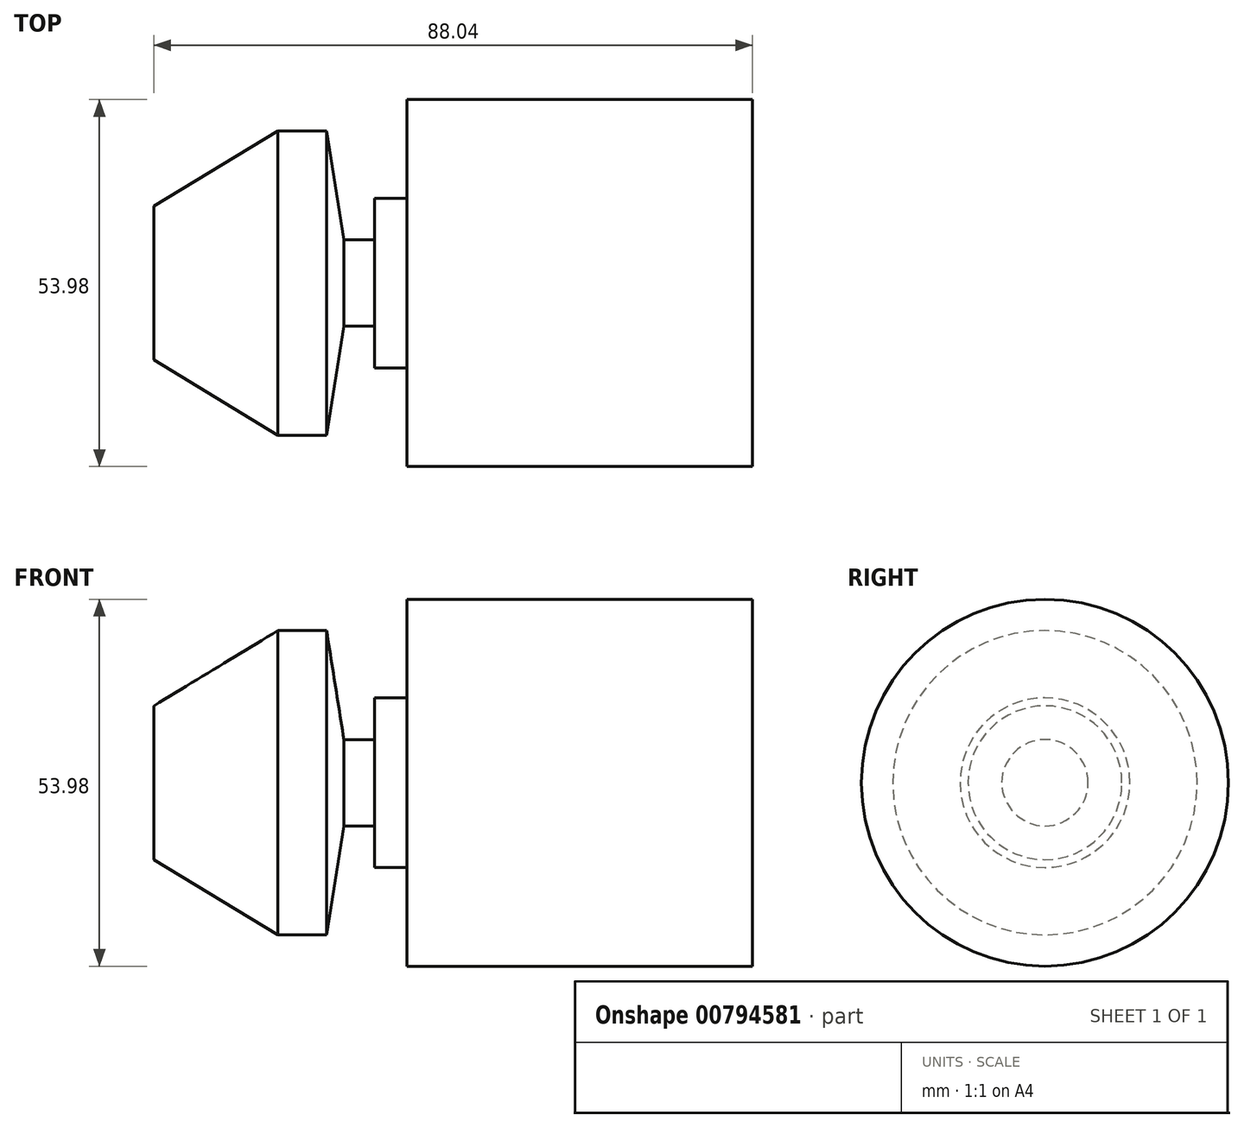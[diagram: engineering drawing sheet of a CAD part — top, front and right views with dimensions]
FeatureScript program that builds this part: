
annotation { "Feature Type Name" : "Feature", "Feature Type Description" : "" }
export const myFeature = defineFeature(function(context is Context, id is Id, definition is map)
    precondition{}
    {
        {
            var Q0;
            Q0=qCreatedBy(makeId("Front.planeOp"),FACE);
            var sketch = newSketch(context, id + "F0", { "sketchPlane" : qUnion([Q0])});
            skLineSegment(sketch, "E0", {"start": v(0, 0) * mm, "end": v(0, 11.3) * mm});
            skLineSegment(sketch, "E1", {"start": v(0, 11.3) * mm, "end": v(18.24, 22.38) * mm});
            skLineSegment(sketch, "E2", {"start": v(18.24, 22.38) * mm, "end": v(25.4, 22.38) * mm});
            skLineSegment(sketch, "E3", {"start": v(25.4, 22.38) * mm, "end": v(27.94, 6.35) * mm});
            skLineSegment(sketch, "E4", {"start": v(27.94, 6.35) * mm, "end": v(32.46, 6.35) * mm});
            skLineSegment(sketch, "E5", {"start": v(32.46, 6.35) * mm, "end": v(32.46, 12.48) * mm});
            skLineSegment(sketch, "E6", {"start": v(32.46, 12.48) * mm, "end": v(37.24, 12.48) * mm});
            skLineSegment(sketch, "E7", {"start": v(37.24, 12.48) * mm, "end": v(37.24, 26.99) * mm});
            skLineSegment(sketch, "E8", {"start": v(37.24, 26.99) * mm, "end": v(88.04, 26.99) * mm});
            skLineSegment(sketch, "E9", {"start": v(88.04, 26.99) * mm, "end": v(88.04, 0) * mm});
            skLineSegment(sketch, "E10", {"start": v(0, 0) * mm, "end": v(88.04, 0) * mm});
            skSolve(sketch);
        }
        {
            var Q0;
            Q0=makeQuery(id+"F0.imprint","IMPRINT",FACE,{"disambiguationData":[TD([[makeQuery(id+"F0.imprint","IMPRINT",EDGE,{"derivedFrom":sQuery(id+"F0.wireOp",EDGE,"E0")}),-1.0]])]});
            var Q1;
            Q1=sQuery(id+"F0.wireOp",EDGE,"E10");
            revolve(context, id + "F1", {"surfaceOperationType" : NewSurfaceOperationType.NEW, "entities" : qUnion([Q0]), "axis" : qUnion([Q1]), "revolveType" : RevolveType.FULL});
        }
    });
